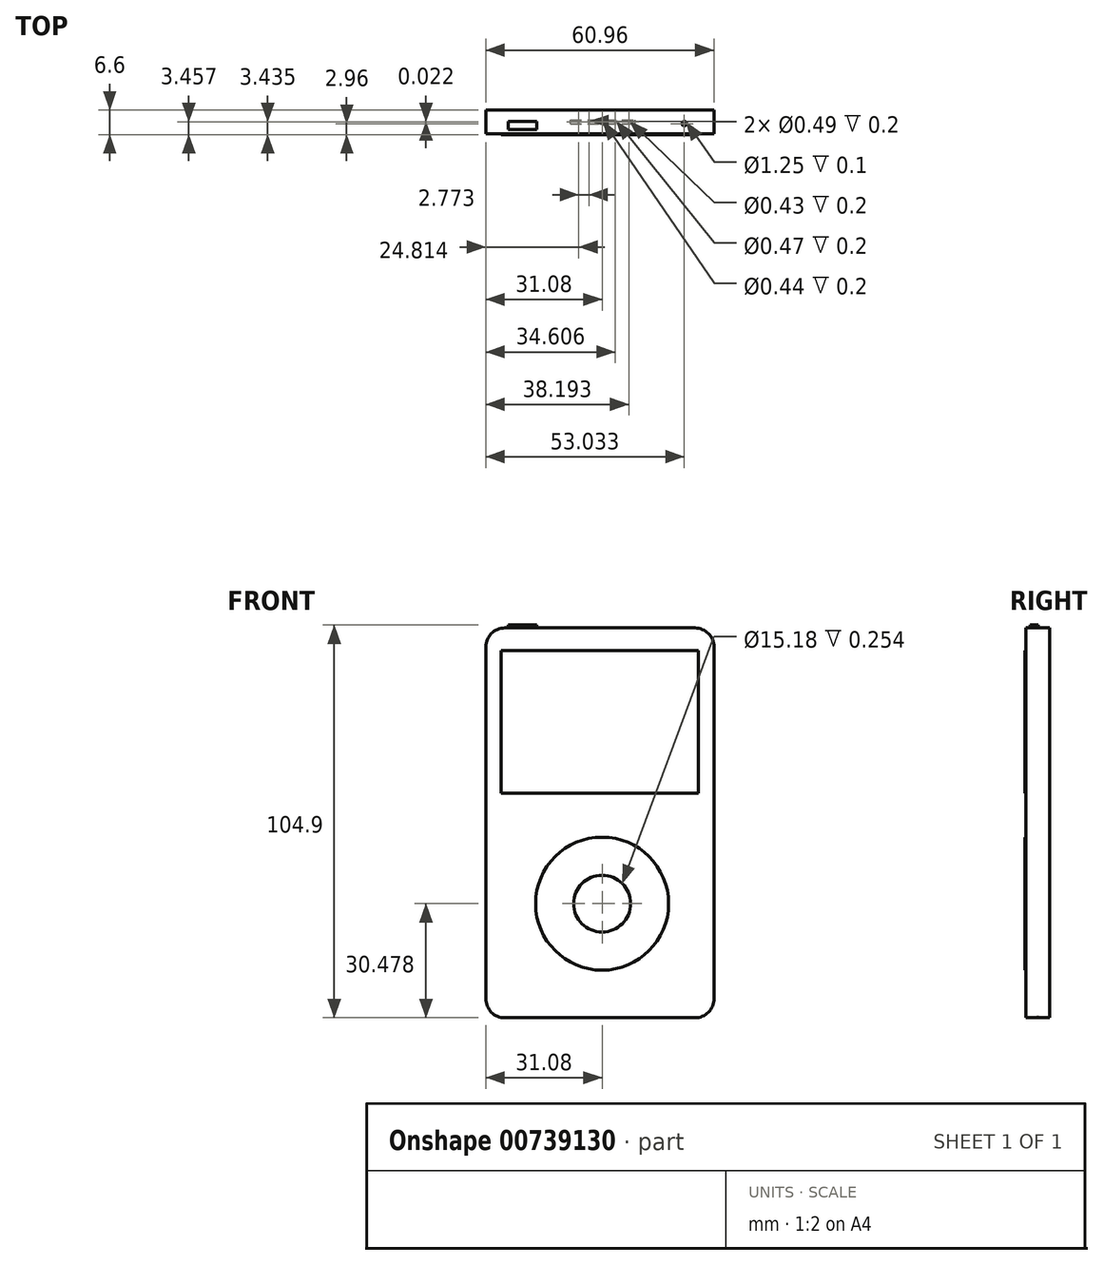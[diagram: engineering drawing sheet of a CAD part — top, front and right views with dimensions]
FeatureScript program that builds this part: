
annotation { "Feature Type Name" : "Feature", "Feature Type Description" : "" }
export const myFeature = defineFeature(function(context is Context, id is Id, definition is map)
    precondition{}
    {
        {
            var Q0;
            Q0=qCreatedBy(makeId("Front.planeOp"),FACE);
            var sketch = newSketch(context, id + "F0", { "sketchPlane" : qUnion([Q0])});
            skLineSegment(sketch, "E0.bottom", {"start": v(-31.08, 59.04) * mm, "end": v(29.88, 59.04) * mm});
            skLineSegment(sketch, "E0.top", {"start": v(-31.08, -45.1) * mm, "end": v(29.88, -45.1) * mm});
            skLineSegment(sketch, "E0.left", {"start": v(-31.08, 59.04) * mm, "end": v(-31.08, -45.1) * mm});
            skLineSegment(sketch, "E0.right", {"start": v(29.88, 59.04) * mm, "end": v(29.88, -45.1) * mm});
            skLineSegment(sketch, "E1.bottom", {"start": v(-26.62, 52.69) * mm, "end": v(25.72, 52.69) * mm});
            skLineSegment(sketch, "E1.top", {"start": v(-26.62, 14.59) * mm, "end": v(25.72, 14.59) * mm});
            skLineSegment(sketch, "E1.left", {"start": v(-26.62, 52.69) * mm, "end": v(-26.62, 14.59) * mm});
            skLineSegment(sketch, "E1.right", {"start": v(25.72, 52.69) * mm, "end": v(25.72, 14.59) * mm});
            skCircle(sketch, "E2", {"center": v(0, -14.62) * mm, "radius": 17.78 * mm});
            skCircle(sketch, "E3", {"center": v(0, -14.62) * mm, "radius": 7.62 * mm});
            skLineSegment(sketch, "E4", {"start": v(-26.62, 52.69) * mm, "end": v(-26.62, 33.64) * mm});
            skSolve(sketch);
        }
        {
            var Q0;
            Q0 = qSketchRegion(id + "F0", true);
            var Q1;
            Q1=makeQuery(id+"F0.imprint","IMPRINT",FACE,{"disambiguationData":[TD([[makeQuery(id+"F0.imprint","IMPRINT",EDGE,{"derivedFrom":sQuery(id+"F0.wireOp",EDGE,"E3")}),1.0]])]});
            var Q2;
            Q2=makeQuery(id+"F0.imprint","IMPRINT",FACE,{"disambiguationData":[TD([[makeQuery(id+"F0.imprint","IMPRINT",EDGE,{"derivedFrom":sQuery(id+"F0.wireOp",EDGE,"E2")}),1.0]])]});
            var Q3;
            Q3=makeQuery(id+"F0.imprint","IMPRINT",FACE,{"disambiguationData":[TD([[makeQuery(id+"F0.imprint","IMPRINT",EDGE,{"derivedFrom":sQuery(id+"F0.wireOp",EDGE,"E1.bottom")}),-1.0]])]});
            extrude(context, id + "F1", {"entities" : qUnion([Q0, Q1, Q2, Q3]), "depth" : 6.35 * mm, "offsetDistance" : 25.4 * mm});
        }
        {
            var Q0;
            Q0=makeQuery(id+"F1.opExtrude","CAP_FACE",FACE,{"disambiguationData":[OSD([sQuery(id+"F0.wireOp",EDGE,"E0.bottom"),sQuery(id+"F0.wireOp",EDGE,"E0.top"),sQuery(id+"F0.wireOp",EDGE,"E0.left"),sQuery(id+"F0.wireOp",EDGE,"E0.right")])],"isStart":false});
            var sketch = newSketch(context, id + "F2", { "sketchPlane" : qUnion([Q0])});
            skCircle(sketch, "E5", {"center": v(0, -14.62) * mm, "radius": 17.77 * mm});
            skCircle(sketch, "E6", {"center": v(0, -14.62) * mm, "radius": 7.59 * mm});
            skSolve(sketch);
        }
        {
            var Q0;
            Q0 = qSketchRegion(id + "F2", true);
            extrude(context, id + "F3", {"entities" : qUnion([Q0]), "operationType" : NewBodyOperationType.ADD, "depth" : 0.25 * mm, "offsetDistance" : 25.4 * mm});
        }
        {
            var Q0;
            {var subQ0=sQuery(id+"F0.wireOp",EDGE,"E0.left");var subQ1=sQuery(id+"F0.wireOp",EDGE,"E0.top");var subQ2=sQuery(id+"F0.wireOp",EDGE,"E0.right");var subQ3=sQuery(id+"F0.wireOp",EDGE,"E0.bottom");Q0=makeQuery(id+"F3.boolean.opBoolean","SPLIT",FACE,{"disambiguationData":[TD([makeQuery(id+"F1.opExtrude","SWEPT_FACE",FACE,{"disambiguationData":[OSD([subQ3])]})])],"derivedFrom":makeQuery(id+"F1.opExtrude","CAP_FACE",FACE,{"disambiguationData":[OSD([subQ3,subQ1,subQ0,subQ2])],"isStart":false})});}
            var sketch = newSketch(context, id + "F4", { "sketchPlane" : qUnion([Q0])});
            skLineSegment(sketch, "E7.bottom", {"start": v(-26.97, 53.04) * mm, "end": v(25.76, 53.04) * mm});
            skLineSegment(sketch, "E7.top", {"start": v(-26.97, 14.94) * mm, "end": v(25.76, 14.94) * mm});
            skLineSegment(sketch, "E7.left", {"start": v(-26.97, 53.04) * mm, "end": v(-26.97, 14.94) * mm});
            skLineSegment(sketch, "E7.right", {"start": v(25.76, 53.04) * mm, "end": v(25.76, 14.94) * mm});
            skSolve(sketch);
        }
        {
            var Q0;
            Q0 = qSketchRegion(id + "F4", true);
            extrude(context, id + "F5", {"entities" : qUnion([Q0]), "operationType" : NewBodyOperationType.ADD, "depth" : 0.25 * mm, "offsetDistance" : 25.4 * mm});
        }
        {
            var Q0;
            Q0=makeQuery(id+"F1.opExtrude","SWEPT_FACE",FACE,{"disambiguationData":[OSD([sQuery(id+"F0.wireOp",EDGE,"E0.bottom")])]});
            var sketch = newSketch(context, id + "F6", { "sketchPlane" : qUnion([Q0])});
            skLineSegment(sketch, "E8.bottom", {"start": v(-25.03, -3.02) * mm, "end": v(-17.51, -3.02) * mm});
            skLineSegment(sketch, "E8.top", {"start": v(-25.03, -5.22) * mm, "end": v(-17.51, -5.22) * mm});
            skLineSegment(sketch, "E8.left", {"start": v(-25.03, -3.02) * mm, "end": v(-25.03, -5.22) * mm});
            skLineSegment(sketch, "E8.right", {"start": v(-17.51, -3.02) * mm, "end": v(-17.51, -5.22) * mm});
            skSolve(sketch);
        }
        {
            var Q0;
            Q0 = qSketchRegion(id + "F6", true);
            extrude(context, id + "F7", {"entities" : qUnion([Q0]), "operationType" : NewBodyOperationType.ADD, "depth" : 0.76 * mm, "offsetDistance" : 25.4 * mm});
        }
        {
            var Q0;
            Q0=makeQuery(id+"F1.opExtrude","SWEPT_EDGE",EDGE,{"disambiguationData":[OSD([sQuery(id+"F0.wireOp",EDGE,"E0.bottom"),sQuery(id+"F0.wireOp",EDGE,"E0.right")])]});
            var Q1;
            Q1=makeQuery(id+"F1.opExtrude","SWEPT_EDGE",EDGE,{"disambiguationData":[OSD([sQuery(id+"F0.wireOp",EDGE,"E0.bottom"),sQuery(id+"F0.wireOp",EDGE,"E0.left")])]});
            var Q2;
            Q2=makeQuery(id+"F1.opExtrude","SWEPT_EDGE",EDGE,{"disambiguationData":[OSD([sQuery(id+"F0.wireOp",EDGE,"E0.top"),sQuery(id+"F0.wireOp",EDGE,"E0.left")])]});
            var Q3;
            Q3=makeQuery(id+"F1.opExtrude","SWEPT_EDGE",EDGE,{"disambiguationData":[OSD([sQuery(id+"F0.wireOp",EDGE,"E0.top"),sQuery(id+"F0.wireOp",EDGE,"E0.right")])]});
            fillet(context, id + "F8", {"entities" : qUnion([Q0, Q1, Q2, Q3]), "radius" : 5.08 * mm, "tangentPropagation" : true, "allowEdgeOverflow" : false});
        }
        {
            var Q0;
            Q0=makeQuery(id+"F1.opExtrude","SWEPT_FACE",FACE,{"disambiguationData":[OSD([sQuery(id+"F0.wireOp",EDGE,"E0.bottom")])]});
            var sketch = newSketch(context, id + "F9", { "sketchPlane" : qUnion([Q0])});
            skCircle(sketch, "E9", {"center": v(21.95, -3.64) * mm, "radius": 0.62 * mm});
            skSolve(sketch);
        }
        {
            var Q0;
            Q0 = qSketchRegion(id + "F9", true);
            extrude(context, id + "F10", {"entities" : qUnion([Q0]), "operationType" : NewBodyOperationType.REMOVE, "oppositeDirection" : true, "depth" : .1 * mm, "offsetDistance" : 25 * mm});
        }
        {
            var Q0;
            Q0=makeQuery(id+"F1.opExtrude","SWEPT_FACE",FACE,{"disambiguationData":[OSD([sQuery(id+"F0.wireOp",EDGE,"E0.top")])]});
            var sketch = newSketch(context, id + "F11", { "sketchPlane" : qUnion([Q0])});
            skLineSegment(sketch, "E10.bottom", {"start": v(-8.5, 3.69) * mm, "end": v(8.84, 3.69) * mm});
            skLineSegment(sketch, "E10.top", {"start": v(-8.5, 2.72) * mm, "end": v(8.84, 2.72) * mm});
            skLineSegment(sketch, "E10.left", {"start": v(-8.5, 3.69) * mm, "end": v(-8.5, 2.72) * mm});
            skLineSegment(sketch, "E10.right", {"start": v(8.84, 3.69) * mm, "end": v(8.84, 2.72) * mm});
            skSolve(sketch);
        }
        {
            var Q0;
            Q0 = qSketchRegion(id + "F11", true);
            extrude(context, id + "F12", {"entities" : qUnion([Q0]), "operationType" : NewBodyOperationType.REMOVE, "oppositeDirection" : true, "depth" : .1 * mm, "offsetDistance" : 25 * mm});
        }
        {
            var Q0;
            Q0=makeQuery(id+"F12.boolean.opBoolean","COPY",FACE,{"derivedFrom":makeQuery(id+"F12.opExtrude","CAP_FACE",FACE,{"disambiguationData":[OSD([sQuery(id+"F11.wireOp",EDGE,"E10.bottom"),sQuery(id+"F11.wireOp",EDGE,"E10.top"),sQuery(id+"F11.wireOp",EDGE,"E10.left"),sQuery(id+"F11.wireOp",EDGE,"E10.right")])],"isStart":false})});
            var sketch = newSketch(context, id + "F13", { "sketchPlane" : qUnion([Q0])});
            skCircle(sketch, "E11", {"center": v(-6.27, 3.16) * mm, "radius": 0.25 * mm});
            skCircle(sketch, "E12", {"center": v(-3.5, 3.14) * mm, "radius": 0.25 * mm});
            skCircle(sketch, "E13", {"center": v(0, 3.14) * mm, "radius": 0.22 * mm});
            skCircle(sketch, "E14", {"center": v(3.53, 3.14) * mm, "radius": 0.23 * mm});
            skCircle(sketch, "E15", {"center": v(7.11, 3.14) * mm, "radius": 0.22 * mm});
            skSolve(sketch);
        }
        {
            var Q0;
            Q0 = qSketchRegion(id + "F13", true);
            extrude(context, id + "F14", {"entities" : qUnion([Q0]), "operationType" : NewBodyOperationType.REMOVE, "oppositeDirection" : true, "depth" : .2 * mm, "offsetDistance" : 25 * mm});
        }
    });
